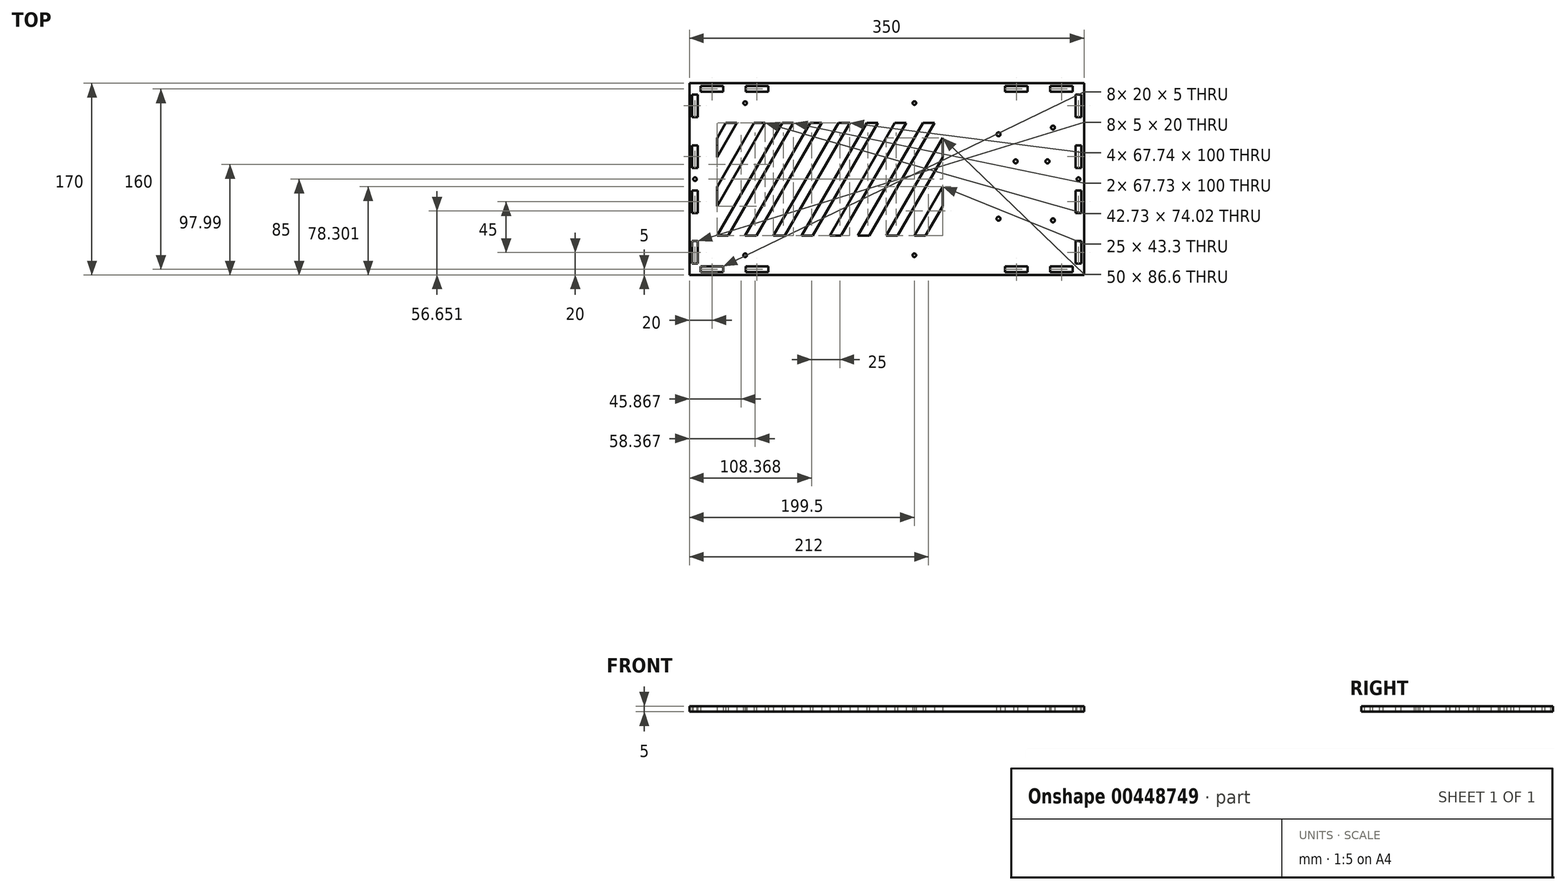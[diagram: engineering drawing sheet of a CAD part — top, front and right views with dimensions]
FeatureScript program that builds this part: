
annotation { "Feature Type Name" : "Feature", "Feature Type Description" : "" }
export const myFeature = defineFeature(function(context is Context, id is Id, definition is map)
    precondition{}
    {
        {
            assignVariable(context, id + "F0", {"name" : "thickness", "anyValue" : 5 * mm});
        }
        {
            var Q0;
            Q0=qCreatedBy(makeId("Top.planeOp"),FACE);
            var sketch = newSketch(context, id + "F1", { "sketchPlane" : qUnion([Q0])});
            skLineSegment(sketch, "E0.bottom", {"start": v(0, 0) * mm, "end": v(350, 0) * mm});
            skLineSegment(sketch, "E0.top", {"start": v(0, 170) * mm, "end": v(350, 170) * mm});
            skLineSegment(sketch, "E0.left", {"start": v(0, 0) * mm, "end": v(0, 170) * mm});
            skLineSegment(sketch, "E0.right", {"start": v(350, 0) * mm, "end": v(350, 170) * mm});
            skLineSegment(sketch, "E1.0", {"start": v(10, 160) * mm, "end": v(340, 160) * mm, "construction": true});
            skLineSegment(sketch, "E1.1", {"start": v(10, 10) * mm, "end": v(10, 160) * mm, "construction": true});
            skLineSegment(sketch, "E1.2", {"start": v(10, 10) * mm, "end": v(340, 10) * mm, "construction": true});
            skLineSegment(sketch, "E1.3", {"start": v(340, 10) * mm, "end": v(340, 160) * mm, "construction": true});
            skLineSegment(sketch, "E2.bottom", {"start": v(325, 34.25) * mm, "end": v(325, 135.75) * mm, "construction": true});
            skLineSegment(sketch, "E2.top", {"start": v(271.5, 34.25) * mm, "end": v(271.5, 135.75) * mm, "construction": true});
            skLineSegment(sketch, "E2.left", {"start": v(325, 34.25) * mm, "end": v(271.5, 34.25) * mm, "construction": true});
            skLineSegment(sketch, "E2.right", {"start": v(325, 135.75) * mm, "end": v(271.5, 135.75) * mm, "construction": true});
            skCircle(sketch, "E3", {"center": v(322.4, 48.45) * mm, "radius": 1.75 * mm});
            skCircle(sketch, "E4", {"center": v(274.1, 49.85) * mm, "radius": 1.75 * mm});
            skCircle(sketch, "E5", {"center": v(289.3, 100.75) * mm, "radius": 1.75 * mm});
            skCircle(sketch, "E6", {"center": v(317.5, 100.75) * mm, "radius": 1.75 * mm});
            skCircle(sketch, "E7", {"center": v(274.1, 124.75) * mm, "radius": 1.75 * mm});
            skCircle(sketch, "E8", {"center": v(322.4, 130.75) * mm, "radius": 1.75 * mm});
            skPoint(sketch, "E9", {"position": v(298.25, 34.25) * mm});
            skPoint(sketch, "E10", {"position": v(325, 85) * mm});
            skPoint(sketch, "E11", {"position": v(340, 85) * mm});
            skLineSegment(sketch, "E12.bottom", {"start": v(17, 142.5) * mm, "end": v(232, 142.5) * mm, "construction": true});
            skLineSegment(sketch, "E12.top", {"start": v(17, 27.5) * mm, "end": v(232, 27.5) * mm, "construction": true});
            skLineSegment(sketch, "E12.left", {"start": v(17, 142.5) * mm, "end": v(17, 27.5) * mm, "construction": true});
            skLineSegment(sketch, "E12.right", {"start": v(232, 142.5) * mm, "end": v(232, 27.5) * mm, "construction": true});
            skPoint(sketch, "E13", {"position": v(232, 85) * mm});
            skCircle(sketch, "E14", {"center": v(199.5, 152.5) * mm, "radius": 1.6 * mm});
            skCircle(sketch, "E15", {"center": v(199.5, 17.5) * mm, "radius": 1.6 * mm});
            skLineSegment(sketch, "E16", {"start": v(199.5, 152.5) * mm, "end": v(199.5, 17.5) * mm, "construction": true});
            skPoint(sketch, "E17", {"position": v(199.5, 85) * mm});
            skCircle(sketch, "E18", {"center": v(49.5, 152.5) * mm, "radius": 1.6 * mm});
            skCircle(sketch, "E19", {"center": v(49.5, 17.5) * mm, "radius": 1.6 * mm});
            skLineSegment(sketch, "E20", {"start": v(49.5, 152.5) * mm, "end": v(49.5, 17.5) * mm, "construction": true});
            skPoint(sketch, "E21", {"position": v(49.5, 85) * mm});
            skLineSegment(sketch, "E22.bottom", {"start": v(10, 7.5) * mm, "end": v(30, 7.5) * mm});
            skLineSegment(sketch, "E22.top", {"start": v(10, 2.5) * mm, "end": v(30, 2.5) * mm});
            skLineSegment(sketch, "E22.left", {"start": v(10, 7.5) * mm, "end": v(10, 2.5) * mm});
            skLineSegment(sketch, "E22.right", {"start": v(30, 7.5) * mm, "end": v(30, 2.5) * mm});
            skPoint(sketch, "E22.middle", {"position": v(20, 5) * mm});
            skLineSegment(sketch, "E23", {"start": v(10, 10) * mm, "end": v(10, 0) * mm, "construction": true});
            skPoint(sketch, "E24", {"position": v(10, 5) * mm});
            skLineSegment(sketch, "E25.bottom", {"start": v(50, 7.5) * mm, "end": v(70, 7.5) * mm});
            skLineSegment(sketch, "E25.top", {"start": v(50, 2.5) * mm, "end": v(70, 2.5) * mm});
            skLineSegment(sketch, "E25.left", {"start": v(50, 7.5) * mm, "end": v(50, 2.5) * mm});
            skLineSegment(sketch, "E25.right", {"start": v(70, 7.5) * mm, "end": v(70, 2.5) * mm});
            skPoint(sketch, "E25.middle", {"position": v(60, 5) * mm});
            skLineSegment(sketch, "E26", {"start": v(175, 10) * mm, "end": v(175, 0) * mm, "construction": true});
            skLineSegment(sketch, "E27.MirrorCS", {"start": v(300, 2.5) * mm, "end": v(280, 2.5) * mm});
            skLineSegment(sketch, "E28.MirrorCS", {"start": v(320, 7.5) * mm, "end": v(320, 2.5) * mm});
            skPoint(sketch, "E29.MirrorP", {"position": v(330, 5) * mm});
            skLineSegment(sketch, "E30.MirrorCS", {"start": v(300, 7.5) * mm, "end": v(280, 7.5) * mm});
            skLineSegment(sketch, "E31.MirrorCS", {"start": v(340, 2.5) * mm, "end": v(320, 2.5) * mm});
            skLineSegment(sketch, "E32.MirrorCS", {"start": v(280, 7.5) * mm, "end": v(280, 2.5) * mm});
            skPoint(sketch, "E33.MirrorP", {"position": v(290, 5) * mm});
            skLineSegment(sketch, "E34.MirrorCS", {"start": v(300, 7.5) * mm, "end": v(300, 2.5) * mm});
            skLineSegment(sketch, "E35.MirrorCS", {"start": v(340, 7.5) * mm, "end": v(340, 2.5) * mm});
            skLineSegment(sketch, "E36.MirrorCS", {"start": v(340, 7.5) * mm, "end": v(320, 7.5) * mm});
            skLineSegment(sketch, "E37", {"start": v(0, 85) * mm, "end": v(350, 85) * mm, "construction": true});
            skLineSegment(sketch, "E38.MirrorCS", {"start": v(30, 162.5) * mm, "end": v(30, 167.5) * mm});
            skPoint(sketch, "E39.MirrorP", {"position": v(20, 165) * mm});
            skLineSegment(sketch, "E40.MirrorCS", {"start": v(10, 167.5) * mm, "end": v(30, 167.5) * mm});
            skLineSegment(sketch, "E41.MirrorCS", {"start": v(10, 162.5) * mm, "end": v(10, 167.5) * mm});
            skPoint(sketch, "E42.MirrorP", {"position": v(10, 165) * mm});
            skLineSegment(sketch, "E43.MirrorCS", {"start": v(10, 162.5) * mm, "end": v(30, 162.5) * mm});
            skLineSegment(sketch, "E44.MirrorCS", {"start": v(50, 167.5) * mm, "end": v(70, 167.5) * mm});
            skLineSegment(sketch, "E45.MirrorCS", {"start": v(50, 162.5) * mm, "end": v(50, 167.5) * mm});
            skLineSegment(sketch, "E46.MirrorCS", {"start": v(50, 162.5) * mm, "end": v(70, 162.5) * mm});
            skPoint(sketch, "E47.MirrorP", {"position": v(60, 165) * mm});
            skLineSegment(sketch, "E48.MirrorCS", {"start": v(70, 162.5) * mm, "end": v(70, 167.5) * mm});
            skLineSegment(sketch, "E49.MirrorCS", {"start": v(300, 167.5) * mm, "end": v(280, 167.5) * mm});
            skLineSegment(sketch, "E50.MirrorCS", {"start": v(280, 162.5) * mm, "end": v(280, 167.5) * mm});
            skLineSegment(sketch, "E51.MirrorCS", {"start": v(340, 167.5) * mm, "end": v(320, 167.5) * mm});
            skPoint(sketch, "E52.MirrorP", {"position": v(290, 165) * mm});
            skPoint(sketch, "E53.MirrorP", {"position": v(330, 165) * mm});
            skLineSegment(sketch, "E54.MirrorCS", {"start": v(340, 162.5) * mm, "end": v(320, 162.5) * mm});
            skLineSegment(sketch, "E55.MirrorCS", {"start": v(320, 162.5) * mm, "end": v(320, 167.5) * mm});
            skLineSegment(sketch, "E56.MirrorCS", {"start": v(300, 162.5) * mm, "end": v(300, 167.5) * mm});
            skLineSegment(sketch, "E57.MirrorCS", {"start": v(300, 162.5) * mm, "end": v(280, 162.5) * mm});
            skLineSegment(sketch, "E58.MirrorCS", {"start": v(340, 162.5) * mm, "end": v(340, 167.5) * mm});
            skLineSegment(sketch, "E59.bottom", {"start": v(7.5, 30) * mm, "end": v(2.5, 30) * mm});
            skLineSegment(sketch, "E59.top", {"start": v(7.5, 10) * mm, "end": v(2.5, 10) * mm});
            skLineSegment(sketch, "E59.left", {"start": v(7.5, 30) * mm, "end": v(7.5, 10) * mm});
            skLineSegment(sketch, "E59.right", {"start": v(2.5, 30) * mm, "end": v(2.5, 10) * mm});
            skPoint(sketch, "E59.middle", {"position": v(5, 20) * mm});
            skLineSegment(sketch, "E60", {"start": v(10, 10) * mm, "end": v(0, 10) * mm, "construction": true});
            skPoint(sketch, "E61", {"position": v(5, 10) * mm});
            skLineSegment(sketch, "E62.bottom", {"start": v(7.5, 75) * mm, "end": v(2.5, 75) * mm});
            skLineSegment(sketch, "E62.top", {"start": v(7.5, 55) * mm, "end": v(2.5, 55) * mm});
            skLineSegment(sketch, "E62.left", {"start": v(7.5, 75) * mm, "end": v(7.5, 55) * mm});
            skLineSegment(sketch, "E62.right", {"start": v(2.5, 75) * mm, "end": v(2.5, 55) * mm});
            skPoint(sketch, "E62.middle", {"position": v(5, 65) * mm});
            skCircle(sketch, "E63", {"center": v(5, 85) * mm, "radius": 1.6 * mm});
            skPoint(sketch, "E63.centerSnap0", {"position": v(5, 75) * mm});
            skLineSegment(sketch, "E64.MirrorCS", {"start": v(7.5, 95) * mm, "end": v(2.5, 95) * mm});
            skPoint(sketch, "E65.MirrorP", {"position": v(5, 105) * mm});
            skLineSegment(sketch, "E66.MirrorCS", {"start": v(7.5, 95) * mm, "end": v(7.5, 115) * mm});
            skLineSegment(sketch, "E67.MirrorCS", {"start": v(7.5, 115) * mm, "end": v(2.5, 115) * mm});
            skLineSegment(sketch, "E68.MirrorCS", {"start": v(2.5, 95) * mm, "end": v(2.5, 115) * mm});
            skLineSegment(sketch, "E69.MirrorCS", {"start": v(7.5, 160) * mm, "end": v(2.5, 160) * mm});
            skLineSegment(sketch, "E70.MirrorCS", {"start": v(2.5, 140) * mm, "end": v(2.5, 160) * mm});
            skLineSegment(sketch, "E71.MirrorCS", {"start": v(7.5, 140) * mm, "end": v(7.5, 160) * mm});
            skLineSegment(sketch, "E72.MirrorCS", {"start": v(7.5, 140) * mm, "end": v(2.5, 140) * mm});
            skPoint(sketch, "E73.MirrorP", {"position": v(5, 150) * mm});
            skLineSegment(sketch, "E74.MirrorCS", {"start": v(342.5, 75) * mm, "end": v(347.5, 75) * mm});
            skCircle(sketch, "E75.MirrorC", {"center": v(345, 85) * mm, "radius": 1.6 * mm});
            skLineSegment(sketch, "E76.MirrorCS", {"start": v(342.5, 10) * mm, "end": v(347.5, 10) * mm});
            skLineSegment(sketch, "E77.MirrorCS", {"start": v(347.5, 30) * mm, "end": v(347.5, 10) * mm});
            skLineSegment(sketch, "E78.MirrorCS", {"start": v(342.5, 95) * mm, "end": v(347.5, 95) * mm});
            skLineSegment(sketch, "E79.MirrorCS", {"start": v(342.5, 95) * mm, "end": v(342.5, 115) * mm});
            skPoint(sketch, "E80.MirrorP", {"position": v(345, 65) * mm});
            skPoint(sketch, "E81.MirrorP", {"position": v(345, 75) * mm});
            skLineSegment(sketch, "E82.MirrorCS", {"start": v(342.5, 115) * mm, "end": v(347.5, 115) * mm});
            skLineSegment(sketch, "E83.MirrorCS", {"start": v(342.5, 160) * mm, "end": v(347.5, 160) * mm});
            skLineSegment(sketch, "E84.MirrorCS", {"start": v(342.5, 30) * mm, "end": v(342.5, 10) * mm});
            skPoint(sketch, "E85.MirrorP", {"position": v(345, 105) * mm});
            skLineSegment(sketch, "E86.MirrorCS", {"start": v(342.5, 75) * mm, "end": v(342.5, 55) * mm});
            skLineSegment(sketch, "E87.MirrorCS", {"start": v(342.5, 30) * mm, "end": v(347.5, 30) * mm});
            skLineSegment(sketch, "E88.MirrorCS", {"start": v(342.5, 140) * mm, "end": v(342.5, 160) * mm});
            skPoint(sketch, "E89.MirrorP", {"position": v(345, 20) * mm});
            skLineSegment(sketch, "E90.MirrorCS", {"start": v(347.5, 75) * mm, "end": v(347.5, 55) * mm});
            skLineSegment(sketch, "E91.MirrorCS", {"start": v(342.5, 55) * mm, "end": v(347.5, 55) * mm});
            skLineSegment(sketch, "E92.MirrorCS", {"start": v(347.5, 140) * mm, "end": v(347.5, 160) * mm});
            skPoint(sketch, "E93.MirrorP", {"position": v(345, 150) * mm});
            skLineSegment(sketch, "E94.MirrorCS", {"start": v(347.5, 95) * mm, "end": v(347.5, 115) * mm});
            skPoint(sketch, "E95.MirrorP", {"position": v(345, 10) * mm});
            skLineSegment(sketch, "E96.MirrorCS", {"start": v(342.5, 140) * mm, "end": v(347.5, 140) * mm});
            skLineSegment(sketch, "E97.bottom", {"start": v(24.5, 35) * mm, "end": v(224.5, 35) * mm, "construction": true});
            skLineSegment(sketch, "E97.top", {"start": v(24.5, 135) * mm, "end": v(224.5, 135) * mm, "construction": true});
            skLineSegment(sketch, "E97.left", {"start": v(24.5, 35) * mm, "end": v(24.5, 135) * mm, "construction": true});
            skLineSegment(sketch, "E97.right", {"start": v(224.5, 35) * mm, "end": v(224.5, 135) * mm, "construction": true});
            skPoint(sketch, "E98", {"position": v(24.5, 85) * mm});
            skPoint(sketch, "E99", {"position": v(124.5, 135) * mm});
            skPoint(sketch, "E100", {"position": v(124.5, 142.5) * mm});
            skLineSegment(sketch, "E101", {"start": v(24.5, 35) * mm, "end": v(82.24, 135) * mm});
            skLineSegment(sketch, "E102", {"start": v(82.24, 135) * mm, "end": v(92.24, 135) * mm});
            skLineSegment(sketch, "E103", {"start": v(92.24, 135) * mm, "end": v(34.5, 35) * mm});
            skLineSegment(sketch, "E104", {"start": v(34.5, 35) * mm, "end": v(24.5, 35) * mm});
            skLineSegment(sketch, "E105.1.0.0", {"start": v(49.5, 35) * mm, "end": v(107.24, 135) * mm});
            skLineSegment(sketch, "E105.1.0.1", {"start": v(117.24, 135) * mm, "end": v(59.5, 35) * mm});
            skLineSegment(sketch, "E105.1.0.2", {"start": v(107.24, 135) * mm, "end": v(117.24, 135) * mm});
            skLineSegment(sketch, "E105.1.0.3", {"start": v(59.5, 35) * mm, "end": v(49.5, 35) * mm});
            skLineSegment(sketch, "E105.2.0.0", {"start": v(74.5, 35) * mm, "end": v(132.24, 135) * mm});
            skLineSegment(sketch, "E105.2.0.1", {"start": v(142.24, 135) * mm, "end": v(84.5, 35) * mm});
            skLineSegment(sketch, "E105.2.0.2", {"start": v(132.24, 135) * mm, "end": v(142.24, 135) * mm});
            skLineSegment(sketch, "E105.2.0.3", {"start": v(84.5, 35) * mm, "end": v(74.5, 35) * mm});
            skLineSegment(sketch, "E105.3.0.0", {"start": v(99.5, 35) * mm, "end": v(157.24, 135) * mm});
            skLineSegment(sketch, "E105.3.0.1", {"start": v(167.24, 135) * mm, "end": v(109.5, 35) * mm});
            skLineSegment(sketch, "E105.3.0.2", {"start": v(157.24, 135) * mm, "end": v(167.24, 135) * mm});
            skLineSegment(sketch, "E105.3.0.3", {"start": v(109.5, 35) * mm, "end": v(99.5, 35) * mm});
            skLineSegment(sketch, "E105.4.0.0", {"start": v(124.5, 35) * mm, "end": v(182.24, 135) * mm});
            skLineSegment(sketch, "E105.4.0.1", {"start": v(192.24, 135) * mm, "end": v(134.5, 35) * mm});
            skLineSegment(sketch, "E105.4.0.2", {"start": v(182.24, 135) * mm, "end": v(192.24, 135) * mm});
            skLineSegment(sketch, "E105.4.0.3", {"start": v(134.5, 35) * mm, "end": v(124.5, 35) * mm});
            skLineSegment(sketch, "E105.5.0.0", {"start": v(149.5, 35) * mm, "end": v(207.24, 135) * mm});
            skLineSegment(sketch, "E105.5.0.1", {"start": v(217.24, 135) * mm, "end": v(159.5, 35) * mm});
            skLineSegment(sketch, "E105.5.0.2", {"start": v(207.24, 135) * mm, "end": v(217.24, 135) * mm});
            skLineSegment(sketch, "E105.5.0.3", {"start": v(159.5, 35) * mm, "end": v(149.5, 35) * mm});
            skLineSegment(sketch, "E105.6.0.0", {"start": v(174.5, 35) * mm, "end": v(224.5, 121.6) * mm});
            skLineSegment(sketch, "E105.6.0.3", {"start": v(184.5, 35) * mm, "end": v(174.5, 35) * mm});
            skLineSegment(sketch, "E105.7.0.0", {"start": v(199.5, 35) * mm, "end": v(224.5, 78.3) * mm});
            skLineSegment(sketch, "E105.7.0.3", {"start": v(209.5, 35) * mm, "end": v(199.5, 35) * mm});
            skLineSegment(sketch, "E105.direction1", {"start": v(24.5, 35) * mm, "end": v(49.5, 35) * mm, "construction": true});
            skLineSegment(sketch, "E106", {"start": v(224.5, 121.6) * mm, "end": v(224.5, 104.1) * mm});
            skLineSegment(sketch, "E107", {"start": v(224.5, 78.3) * mm, "end": v(224.5, 60.91) * mm});
            skLineSegment(sketch, "E108.trimOffspring", {"start": v(224.5, 104.1) * mm, "end": v(184.5, 35) * mm});
            skLineSegment(sketch, "E109.trimOffspring", {"start": v(224.5, 60.91) * mm, "end": v(209.5, 35) * mm});
            skLineSegment(sketch, "E110.1.0.1", {"start": v(67.24, 135) * mm, "end": v(24.5, 60.98) * mm});
            skLineSegment(sketch, "E110.1.0.2", {"start": v(57.24, 135) * mm, "end": v(67.24, 135) * mm});
            skLineSegment(sketch, "E110.1.0.3", {"start": v(9.5, 35) * mm, "end": v(-0.5, 35) * mm});
            skLineSegment(sketch, "E110.2.0.1", {"start": v(42.24, 135) * mm, "end": v(24.5, 104.28) * mm});
            skLineSegment(sketch, "E110.2.0.2", {"start": v(32.24, 135) * mm, "end": v(42.24, 135) * mm});
            skLineSegment(sketch, "E110.direction1", {"start": v(24.5, 35) * mm, "end": v(-0.5, 35) * mm, "construction": true});
            skLineSegment(sketch, "E111.trimOffspring", {"start": v(24.5, 121.37) * mm, "end": v(32.24, 135) * mm});
            skLineSegment(sketch, "E112.trimOffspring", {"start": v(24.5, 78.19) * mm, "end": v(57.24, 135) * mm});
            skLineSegment(sketch, "E113", {"start": v(24.5, 121.37) * mm, "end": v(24.5, 104.28) * mm});
            skLineSegment(sketch, "E114", {"start": v(24.5, 78.19) * mm, "end": v(24.5, 60.98) * mm});
            skSolve(sketch);
        }
        {
            var Q0;
            Q0=qSketchRegion(id+"F1",true);
            extrude(context, id + "F2", {"entities" : qUnion([Q0]), "depth" : getVariable(context, 'thickness')});
        }
    });
